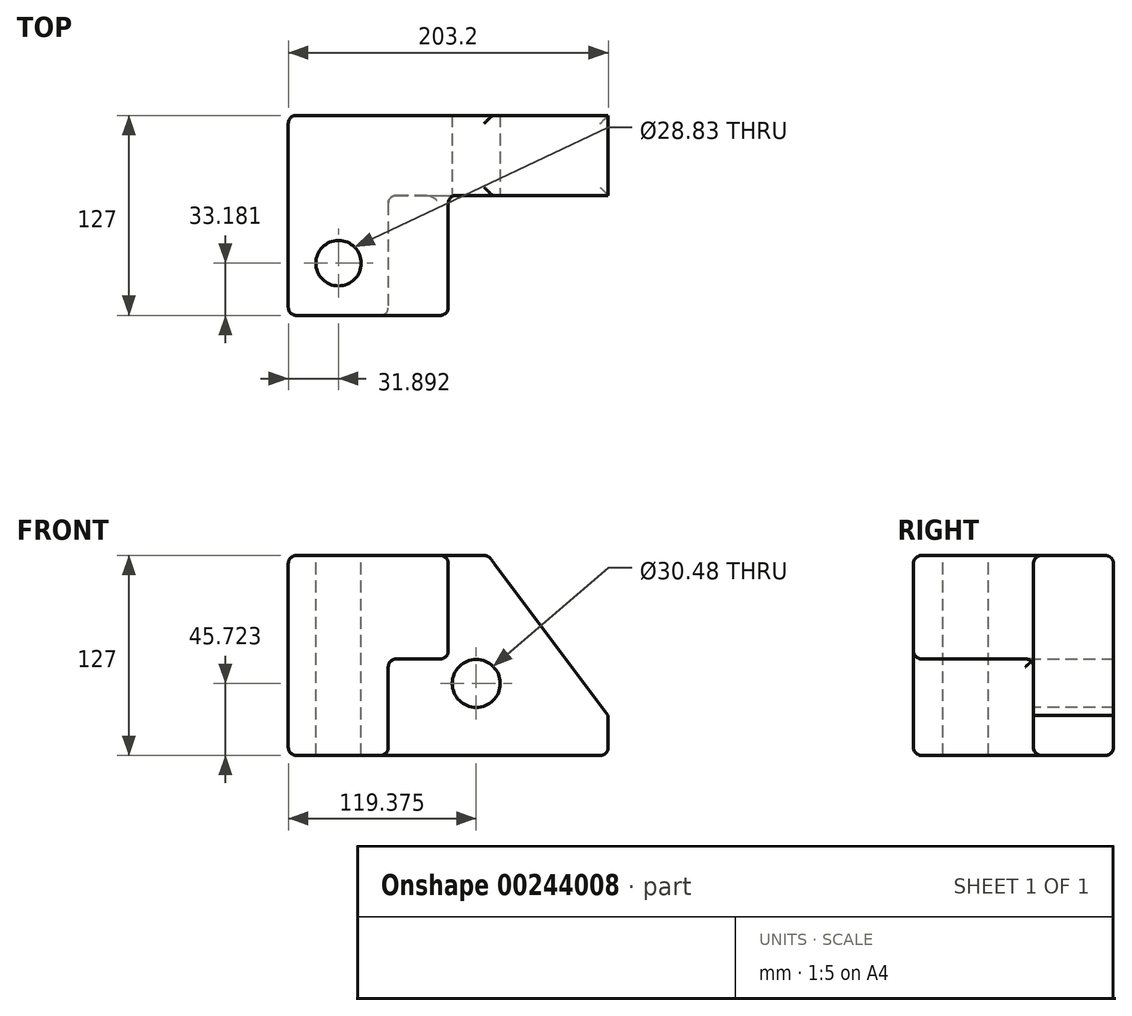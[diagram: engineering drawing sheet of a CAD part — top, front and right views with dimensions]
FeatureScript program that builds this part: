
annotation { "Feature Type Name" : "Feature", "Feature Type Description" : "" }
export const myFeature = defineFeature(function(context is Context, id is Id, definition is map)
    precondition{}
    {
        {
            var Q0;
            Q0=qCreatedBy(makeId("Front.planeOp"),FACE);
            var sketch = newSketch(context, id + "F0", { "sketchPlane" : qUnion([Q0])});
            skLineSegment(sketch, "E0.bottom", {"start": v(-108.05, 65.72) * mm, "end": v(95.15, 65.72) * mm});
            skLineSegment(sketch, "E0.top", {"start": v(-108.05, -61.28) * mm, "end": v(95.15, -61.28) * mm});
            skLineSegment(sketch, "E0.left", {"start": v(-108.05, 65.72) * mm, "end": v(-108.05, -61.28) * mm});
            skLineSegment(sketch, "E0.right", {"start": v(95.15, 65.72) * mm, "end": v(95.15, -61.28) * mm});
            skSolve(sketch);
        }
        {
            var Q0;
            Q0=makeQuery(id+"F0.imprint","IMPRINT",FACE,{"disambiguationData":[TD([[makeQuery(id+"F0.imprint","IMPRINT",EDGE,{"derivedFrom":sQuery(id+"F0.wireOp",EDGE,"E0.bottom")}),-1.0]])]});
            extrude(context, id + "F1", {"entities" : qUnion([Q0]), "depth" : 127 * mm});
        }
        {
            var Q0;
            Q0=makeQuery(id+"F1.opExtrude","CAP_FACE",FACE,{"disambiguationData":[OSD([sQuery(id+"F0.wireOp",EDGE,"E0.bottom"),sQuery(id+"F0.wireOp",EDGE,"E0.top"),sQuery(id+"F0.wireOp",EDGE,"E0.left"),sQuery(id+"F0.wireOp",EDGE,"E0.right")])],"isStart":false});
            var sketch = newSketch(context, id + "F2", { "sketchPlane" : qUnion([Q0])});
            skLineSegment(sketch, "E1", {"start": v(-108.05, 65.72) * mm, "end": v(-6.45, 65.72) * mm});
            skLineSegment(sketch, "E2", {"start": v(-6.45, 65.72) * mm, "end": v(-6.45, 0) * mm});
            skLineSegment(sketch, "E3", {"start": v(-6.45, 0) * mm, "end": v(-44.55, 0) * mm});
            skLineSegment(sketch, "E4", {"start": v(-44.55, 0) * mm, "end": v(-44.55, -61.28) * mm});
            skLineSegment(sketch, "E5", {"start": v(-44.55, -61.28) * mm, "end": v(-108.05, -61.28) * mm});
            skLineSegment(sketch, "E6", {"start": v(-108.05, -61.28) * mm, "end": v(-108.05, 65.72) * mm});
            skSolve(sketch);
        }
        {
            var Q0;
            {var subQ2=sQuery(id+"F2.wireOp",EDGE,"E2");Q0=makeQuery(id+"F2.imprint","IMPRINT",FACE,{"disambiguationData":[TD([[makeQuery(id+"F2.imprint","IMPRINT",EDGE,{"derivedFrom":subQ2}),1.0]])]});}
            extrude(context, id + "F3", {"entities" : qUnion([Q0]), "operationType" : NewBodyOperationType.REMOVE, "oppositeDirection" : true, "depth" : 76.2 * mm});
        }
        {
            var Q0;
            Q0=makeQuery(id+"F1.opExtrude","SWEPT_EDGE",EDGE,{"disambiguationData":[OSD([sQuery(id+"F0.wireOp",EDGE,"E0.bottom"),sQuery(id+"F0.wireOp",EDGE,"E0.right")])]});
            chamfer(context, id + "F4", {"entities" : qUnion([Q0]), "chamferType" : ChamferType.TWO_OFFSETS, "width1" : 76.2 * mm, "oppositeDirection" : false, "width2" : 101.6 * mm, "tangentPropagation" : true});
        }
        {
            var Q0;
            Q0=makeQuery(id+"F3.boolean.opBoolean","COPY",EDGE,{"derivedFrom":makeQuery(id+"F3.opExtrude","SWEPT_EDGE",EDGE,{"disambiguationData":[OSD([sQuery(id+"F0.wireOp",EDGE,"E0.bottom"),sQuery(id+"F2.wireOp",EDGE,"E1"),sQuery(id+"F2.wireOp",EDGE,"E2")])]})});
            var Q1;
            Q1=makeQuery(id+"F1.opExtrude","CAP_EDGE",EDGE,{"disambiguationData":[OSD([sQuery(id+"F0.wireOp",EDGE,"E0.bottom")])],"isStart":false});
            var Q2;
            Q2=makeQuery(id+"F3.boolean.opBoolean","COPY",EDGE,{"derivedFrom":makeQuery(id+"F3.opExtrude","CAP_EDGE",EDGE,{"disambiguationData":[OSD([sQuery(id+"F2.wireOp",EDGE,"E2")])],"isStart":true})});
            var Q3;
            Q3=makeQuery(id+"F3.boolean.opBoolean","COPY",EDGE,{"derivedFrom":makeQuery(id+"F3.opExtrude","SWEPT_EDGE",EDGE,{"disambiguationData":[OSD([sQuery(id+"F2.wireOp",EDGE,"E2"),sQuery(id+"F2.wireOp",EDGE,"E3")])]})});
            var Q4;
            Q4=makeQuery(id+"F3.boolean.opBoolean","COPY",EDGE,{"derivedFrom":makeQuery(id+"F3.opExtrude","CAP_EDGE",EDGE,{"disambiguationData":[OSD([sQuery(id+"F2.wireOp",EDGE,"E2")])],"isStart":false})});
            var Q5;
            {var subQ0=sQuery(id+"F0.wireOp",EDGE,"E0.bottom");Q5=makeQuery(id+"F4.opChamfer","BLEND_EDGE",EDGE,{"blendedFrom":[makeQuery(id+"F1.opExtrude","SWEPT_EDGE",EDGE,{"disambiguationData":[OSD([subQ0,sQuery(id+"F0.wireOp",EDGE,"E0.right")])]}),makeQuery(id+"F1.opExtrude","SWEPT_FACE",FACE,{"disambiguationData":[OSD([subQ0])]})],"blendedInto":[makeQuery(id+"F1.opExtrude","SWEPT_FACE",FACE,{"disambiguationData":[OSD([subQ0])]})]});}
            var Q6;
            Q6=makeQuery(id+"F1.opExtrude","CAP_EDGE",EDGE,{"disambiguationData":[OSD([sQuery(id+"F0.wireOp",EDGE,"E0.bottom")])],"isStart":true});
            var Q7;
            Q7=makeQuery(id+"F1.opExtrude","SWEPT_FACE",FACE,{"disambiguationData":[OSD([sQuery(id+"F0.wireOp",EDGE,"E0.bottom")])]});
            var Q8;
            Q8=makeQuery(id+"F1.opExtrude","CAP_FACE",FACE,{"disambiguationData":[OSD([sQuery(id+"F0.wireOp",EDGE,"E0.bottom"),sQuery(id+"F0.wireOp",EDGE,"E0.top"),sQuery(id+"F0.wireOp",EDGE,"E0.left"),sQuery(id+"F0.wireOp",EDGE,"E0.right")])],"isStart":false});
            var Q9;
            Q9=makeQuery(id+"F3.boolean.opBoolean","COPY",FACE,{"derivedFrom":makeQuery(id+"F3.opExtrude","SWEPT_FACE",FACE,{"disambiguationData":[OSD([sQuery(id+"F2.wireOp",EDGE,"E4")])]})});
            var Q10;
            Q10=makeQuery(id+"F1.opExtrude","SWEPT_FACE",FACE,{"disambiguationData":[OSD([sQuery(id+"F0.wireOp",EDGE,"E0.top")])]});
            var Q11;
            Q11=makeQuery(id+"F1.opExtrude","SWEPT_FACE",FACE,{"disambiguationData":[OSD([sQuery(id+"F0.wireOp",EDGE,"E0.left")])]});
            fillet(context, id + "F5", {"entities" : qUnion([Q0, Q1, Q2, Q3, Q4, Q5, Q6, Q7, Q8, Q9, Q10, Q11]), "radius" : 5.08 * mm, "tangentPropagation" : true, "allowEdgeOverflow" : false});
        }
        {
            var Q0;
            Q0=makeQuery(id+"F3.boolean.opBoolean","COPY",FACE,{"derivedFrom":makeQuery(id+"F3.opExtrude","CAP_FACE",FACE,{"disambiguationData":[OSD([sQuery(id+"F0.wireOp",EDGE,"E0.bottom"),sQuery(id+"F0.wireOp",EDGE,"E0.top"),sQuery(id+"F0.wireOp",EDGE,"E0.right"),sQuery(id+"F2.wireOp",EDGE,"E2"),sQuery(id+"F2.wireOp",EDGE,"E3"),sQuery(id+"F2.wireOp",EDGE,"E4")])],"isStart":false})});
            var sketch = newSketch(context, id + "F6", { "sketchPlane" : qUnion([Q0])});
            skCircle(sketch, "E7", {"center": v(11.33, -15.56) * mm, "radius": 15.24 * mm});
            skSolve(sketch);
        }
        {
            var Q0;
            Q0=makeQuery(id+"F6.imprint","IMPRINT",FACE,{"disambiguationData":[TD([[makeQuery(id+"F6.imprint","IMPRINT",EDGE,{"derivedFrom":sQuery(id+"F6.wireOp",EDGE,"E7")}),1.0]])]});
            var Q1;
            Q1=makeQuery(id+"F1.opExtrude","CAP_FACE",FACE,{"disambiguationData":[OSD([sQuery(id+"F0.wireOp",EDGE,"E0.bottom"),sQuery(id+"F0.wireOp",EDGE,"E0.top"),sQuery(id+"F0.wireOp",EDGE,"E0.left"),sQuery(id+"F0.wireOp",EDGE,"E0.right")])],"isStart":true});
            extrude(context, id + "F7", {"entities" : qUnion([Q0]), "operationType" : NewBodyOperationType.REMOVE, "endBound" : BoundingType.UP_TO_SURFACE, "oppositeDirection" : true, "endBoundEntityFace" : qUnion([Q1]), "depth" : 25.4 * mm});
        }
        {
            var Q0;
            Q0=makeQuery(id+"F1.opExtrude","SWEPT_FACE",FACE,{"disambiguationData":[OSD([sQuery(id+"F0.wireOp",EDGE,"E0.bottom")])]});
            var sketch = newSketch(context, id + "F8", { "sketchPlane" : qUnion([Q0])});
            skCircle(sketch, "E8", {"center": v(-76.16, -93.82) * mm, "radius": 14.42 * mm});
            skSolve(sketch);
        }
        {
            var Q0;
            Q0=makeQuery(id+"F8.imprint","IMPRINT",FACE,{"disambiguationData":[TD([[makeQuery(id+"F8.imprint","IMPRINT",EDGE,{"derivedFrom":sQuery(id+"F8.wireOp",EDGE,"E8")}),1.0]])]});
            var Q1;
            Q1=makeQuery(id+"F1.opExtrude","SWEPT_FACE",FACE,{"disambiguationData":[OSD([sQuery(id+"F0.wireOp",EDGE,"E0.top")])]});
            extrude(context, id + "F9", {"entities" : qUnion([Q0]), "operationType" : NewBodyOperationType.REMOVE, "endBound" : BoundingType.UP_TO_SURFACE, "oppositeDirection" : true, "endBoundEntityFace" : qUnion([Q1]), "depth" : 25.4 * mm});
        }
    });
